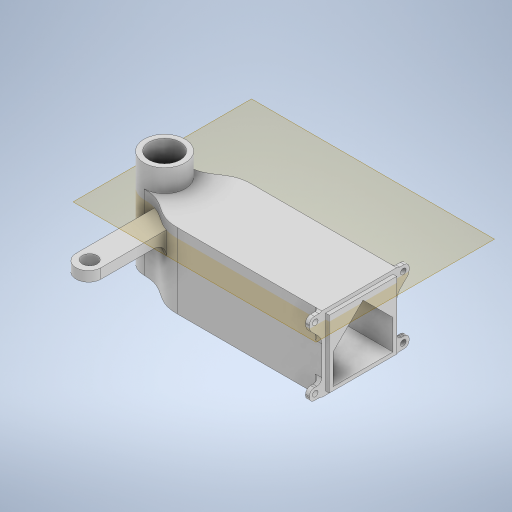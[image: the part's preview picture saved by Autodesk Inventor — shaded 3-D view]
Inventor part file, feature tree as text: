
AUTODESK INVENTOR PART (.ipt)
format: ipt  version: 2024 (Build 280153000, 153)  size: 544,768 bytes
history: native  units: in
note: dims shown in document units (in); Inventor stores cm internally (conversion verified against a paired STEP export)
features: extrude x8, sketch x7, fillet x5, projected_geometry x3, plane x2, hole x1, chamfer x1
ambient origin geometry x8: Origin, YZ Plane, XZ Plane, XY Plane, X Axis, Y Axis, Z Axis, Center Point
bodies: Solid1 (feature_tree)
feature tree (27):
  extrude  "Extrusion1"  Depth=0.0787in
  plane  "Work Plane1"
  extrude  "Extrusion2"  Depth=0.374in
  sketch  "Sketch4"  dims[d5=1.1811in d6=0.1181in]
  extrude  "Extrusion4"  Depth=0.1181in
  hole  "Hole2"  [1 undecoded]
  sketch  "Sketch9"  dims[d10=0.4724in d11=0.1181in]
  extrude  "Extrusion7"  Depth=0.1181in
  extrude  "Extrusion8"  Depth=1.1811in
  extrude  "Extrusion9"  Depth=0.0394in TaperAngle=0.0deg
  extrude  "Extrusion3"  Depth=0.0394in
  fillet  "Fillet1"  Radius=1.1811in
  chamfer  "Chamfer1"  Distance=1.1811in
  fillet  "Fillet2"  Radius=0.0591in
  plane  "Work Plane3"
  extrude  "Extrusion10"  Depth=0.0394in TaperAngle=0.0deg
  fillet  "Fillet3"  Radius=0.0591in
  fillet  "Fillet4"  Radius=0.748in
  fillet  "Fillet5"  Radius=0.5906in
  sketch  "Sketch1"  dims[d0=0.6496in d1=0.0787in]
  sketch  "Sketch2"  dims[d2=0.4724in d3=0.0in d4=0.374in]
  projected_geometry  "Projected Loop1"
  sketch  "Sketch8"  dims[d7=0.1181in d9=0.9449in]
  projected_geometry  "Projected Loop5"
  sketch  "Sketch11"  dims[d12=0.1181in d13=1.1811in]
  sketch  "Sketch12"  dims[d20=0.1181in d23=2.7559in d24=0.0in d25=0.0886in d26=1.1811in d27=1.1811in d35=0.0591in d36=0.2362in d37=0.0in d38=0.0591in d39=0.0in d40=0.748in d41=0.0in d53=0.5906in d54=0.1033in d55=0.1033in d56=0.1033in d57=0.1033in d58=0.1033in d60=0.1033in d61=0.1033in d62=0.5906in d63=0.2362in d64=0.1575in d65=0.0787in d66=90.0deg d67=0.3937in d68=0.8108in d69=0.7874in d70=0.0787in d71=0.0787in d72=0.0in d73=0.0in d74=1.1811in d75=0.0in d76=0.1033in d77=0.1033in d78=0.1033in d79=0.1033in d80=0.1772in d82=0.1772in d86=0.0591in d87=0.0in d91=0.0787in d92=0.0148in d93=0.0886in d94=0.1969in d95=0.1969in d99=0.0148in d100=0.1772in d101=0.0787in d102=45.0deg d103=0.1969in d104=0.4724in d105=0.4724in d106=0.4724in d107=0.2362in d108=0.3937in d109=1.5748in d110=0.3937in d111=0.1969in d113=0.2165in d114=0.1575in d115=0.0in d116=0.1969in d117=0.1969in d119=-0.0295in d120=0.0394in]
  projected_geometry  "Projected Loop6"
note: 1 required parameter value undecoded (feature->parameter linkage not recoverable at this tier; creation-order binding heuristic only, values carry confidence <= 0.55)
